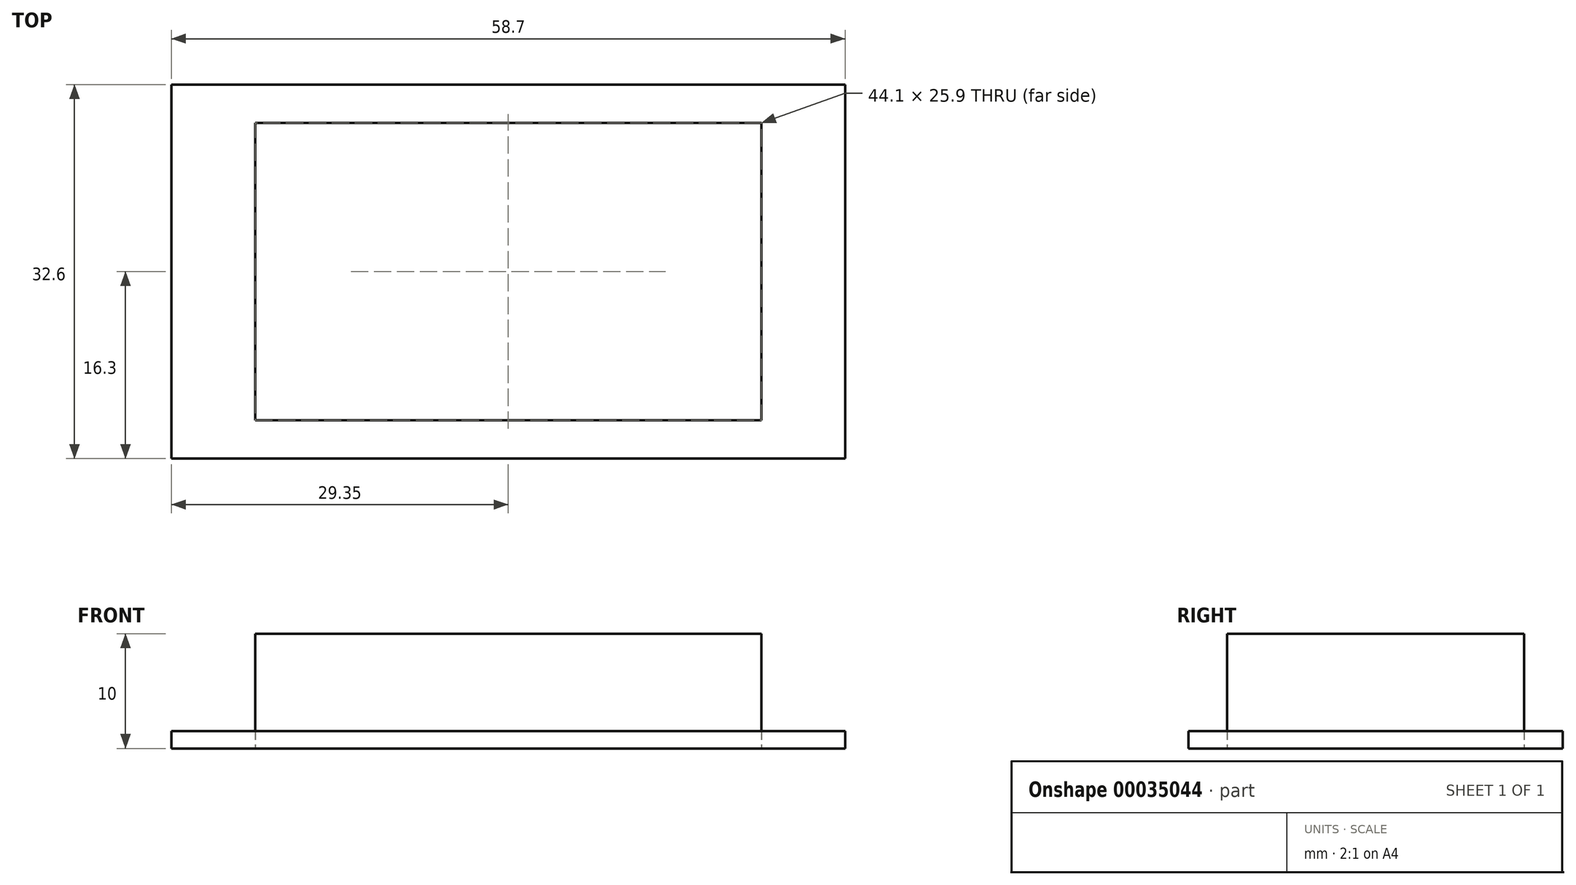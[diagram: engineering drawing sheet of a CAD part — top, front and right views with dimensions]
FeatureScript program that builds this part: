
annotation { "Feature Type Name" : "Feature", "Feature Type Description" : "" }
export const myFeature = defineFeature(function(context is Context, id is Id, definition is map)
    precondition{}
    {
        {
            var Q0;
            Q0=qCreatedBy(makeId("Top.planeOp"),FACE);
            var sketch = newSketch(context, id + "F0", { "sketchPlane" : qUnion([Q0])});
            skLineSegment(sketch, "E0.rect.bottom", {"start": v(29.35, -16.3) * mm, "end": v(-29.35, -16.3) * mm});
            skLineSegment(sketch, "E0.rect.top", {"start": v(29.35, 16.3) * mm, "end": v(-29.35, 16.3) * mm});
            skLineSegment(sketch, "E0.rect.left", {"start": v(29.35, -16.3) * mm, "end": v(29.35, 16.3) * mm});
            skLineSegment(sketch, "E0.rect.right", {"start": v(-29.35, -16.3) * mm, "end": v(-29.35, 16.3) * mm});
            skPoint(sketch, "E0.rect.middle", {"position": v(0, 0) * mm});
            skLineSegment(sketch, "E1.1", {"start": v(22.05, -12.95) * mm, "end": v(-22.05, -12.95) * mm});
            skLineSegment(sketch, "E1.2", {"start": v(22.05, -12.95) * mm, "end": v(22.05, 12.95) * mm});
            skLineSegment(sketch, "E1.3", {"start": v(22.05, 12.95) * mm, "end": v(-22.05, 12.95) * mm});
            skLineSegment(sketch, "E2", {"start": v(-22.05, 12.95) * mm, "end": v(-22.05, -12.95) * mm});
            skSolve(sketch);
        }
        {
            var Q0;
            Q0=makeQuery(id+"F0.imprint","IMPRINT",FACE,{"disambiguationData":[TD([[makeQuery(id+"F0.imprint","IMPRINT",EDGE,{"derivedFrom":sQuery(id+"F0.wireOp",EDGE,"E0.rect.bottom")}),-1.0]])]});
            extrude(context, id + "F1", {"entities" : qUnion([Q0]), "depth" : 1.5 * mm});
        }
        {
            var Q0;
            Q0=makeQuery(id+"F1.opExtrude","CAP_FACE",FACE,{"disambiguationData":[OSD([sQuery(id+"F0.wireOp",EDGE,"E0.rect.bottom"),sQuery(id+"F0.wireOp",EDGE,"E0.rect.top"),sQuery(id+"F0.wireOp",EDGE,"E0.rect.left"),sQuery(id+"F0.wireOp",EDGE,"E0.rect.right"),sQuery(id+"F0.wireOp",EDGE,"E1.1"),sQuery(id+"F0.wireOp",EDGE,"E1.2"),sQuery(id+"F0.wireOp",EDGE,"E1.3"),sQuery(id+"F0.wireOp",EDGE,"E2")])],"isStart":false});
            var sketch = newSketch(context, id + "F2", { "sketchPlane" : qUnion([Q0])});
            skLineSegment(sketch, "E3.bottom", {"start": v(-22.05, 12.95) * mm, "end": v(22.05, 12.95) * mm});
            skLineSegment(sketch, "E3.top", {"start": v(-22.05, -12.95) * mm, "end": v(22.05, -12.95) * mm});
            skLineSegment(sketch, "E3.left", {"start": v(-22.05, 12.95) * mm, "end": v(-22.05, -12.95) * mm});
            skLineSegment(sketch, "E3.right", {"start": v(22.05, 12.95) * mm, "end": v(22.05, -12.95) * mm});
            skSolve(sketch);
        }
        {
            var Q0;
            Q0=makeQuery(id+"F2.imprint","IMPRINT",FACE,{"disambiguationData":[TD([[makeQuery(id+"F2.imprint","IMPRINT",EDGE,{"derivedFrom":sQuery(id+"F2.wireOp",EDGE,"E3.bottom")}),1.0]])]});
            extrude(context, id + "F3", {"entities" : qUnion([Q0]), "depth" : 8.5 * mm});
        }
    });
